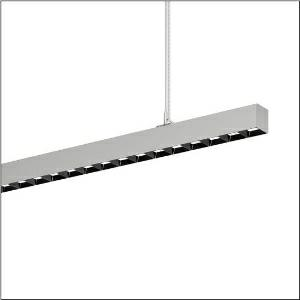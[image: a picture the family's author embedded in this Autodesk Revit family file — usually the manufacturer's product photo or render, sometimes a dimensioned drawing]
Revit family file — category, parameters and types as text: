
# Revit family: silica_r__21_51mx32dc4dsb_d767
name_source: partatom
category: Lighting Fixtures
units: mm (PartAtom-declared; Revit-internal decimal feet)

## family parameters
Cut with Voids When Loaded = No
Host = Face
Light Source = No
Part Type = Normal
Room Calculation Point = No
Round Connector Dimension = Use Diameter
Shared = No

## types (1)
- --- (1 x LED, 18230 lm, 105.8 W, 4000K)
    Apparent Load = 106 VA
    CIE Flux Codes = 86 99 100 59 100
    Color Rendering = 80
    Color Temperature = 4000K
    Default Elevation = 1800 mm
    Description = Silica® 21, office luminaire, primary light control with darklight reflector, of PMMA, black, CAT 2 (L<= 3000cd/m²), light emission: direct/indirect distribution, primary light characteristic: symmetric, installation type: suspended mounting, LED, rated luminous flux: 18.230lm, luminous efficacy: 172lm/W, light colour: 840, colour temperature: 4000K, control gear: DALI 2, with terminal, 3+2-pole, max. 2.5mm², mains connection: 220..240V, AC, 50/60Hz, rated input power: 105.8W, luminaire housing, of aluminium, metallic grey (RAL 9006), length: 3.004mm, width: 53mm, height: 53mm, protection rating (complete): IP20, insulation class (complete): insulation class I (protective earthing), certification: CE, permissible operating ambient temperature: 0..+35°C, standard: EN 50419, packaging unit: 1 piece
    Height = 53 mm
    Lamp = 1 x LED
    Lamp Light Flux = 18230 lm
    Lamp Power = 105.8 W
    Lamp count = 1
    Length = 3004 mm
    Luminous efficacy = 172 lm/W
    Manufacturer = Siteco
    ModVariant = No
    Model = 51MX32DC4DSB
    Mounting Place = Ceiling
    Mounting Type = Pendant
    Number of Poles = 1
    OnlyDefault = Yes
    Power Factor = 1
    Product Name = Silica® 21
    Product group = office luminaire | ceiling pendant
    ProductGroupID = 904
    Protection Class = Protection class I
    Protection Degree = IP 20
    RLX_Detail_Level = 1
    RLX_Emergency_Light_Flux = 0 lm
    RLX_Emergency_Type = 0
    RLX_Emergency_Type_DB = No
    RlxData = <blob elided: 65701 chars, md5=74156722>
    Socket = socket
    Standby Power = 0 W
    System Light Flux = 18230 lm
    System Power = 106 W
    Type Comments = factory setting: luminous flux: 100 % | dim-lin: 254 | 366 mA
    Type Image = l_1335859.jpg
    URL = http://relux.com
    VarID = @adj_121984
    Voltage = 0 V
    Weight = 0.00 kg
    Width = 53 mm

## geometry (parser evidence)
native form markers: Blend x4, Sweep x14
no freeform markers — native parametric forms only
